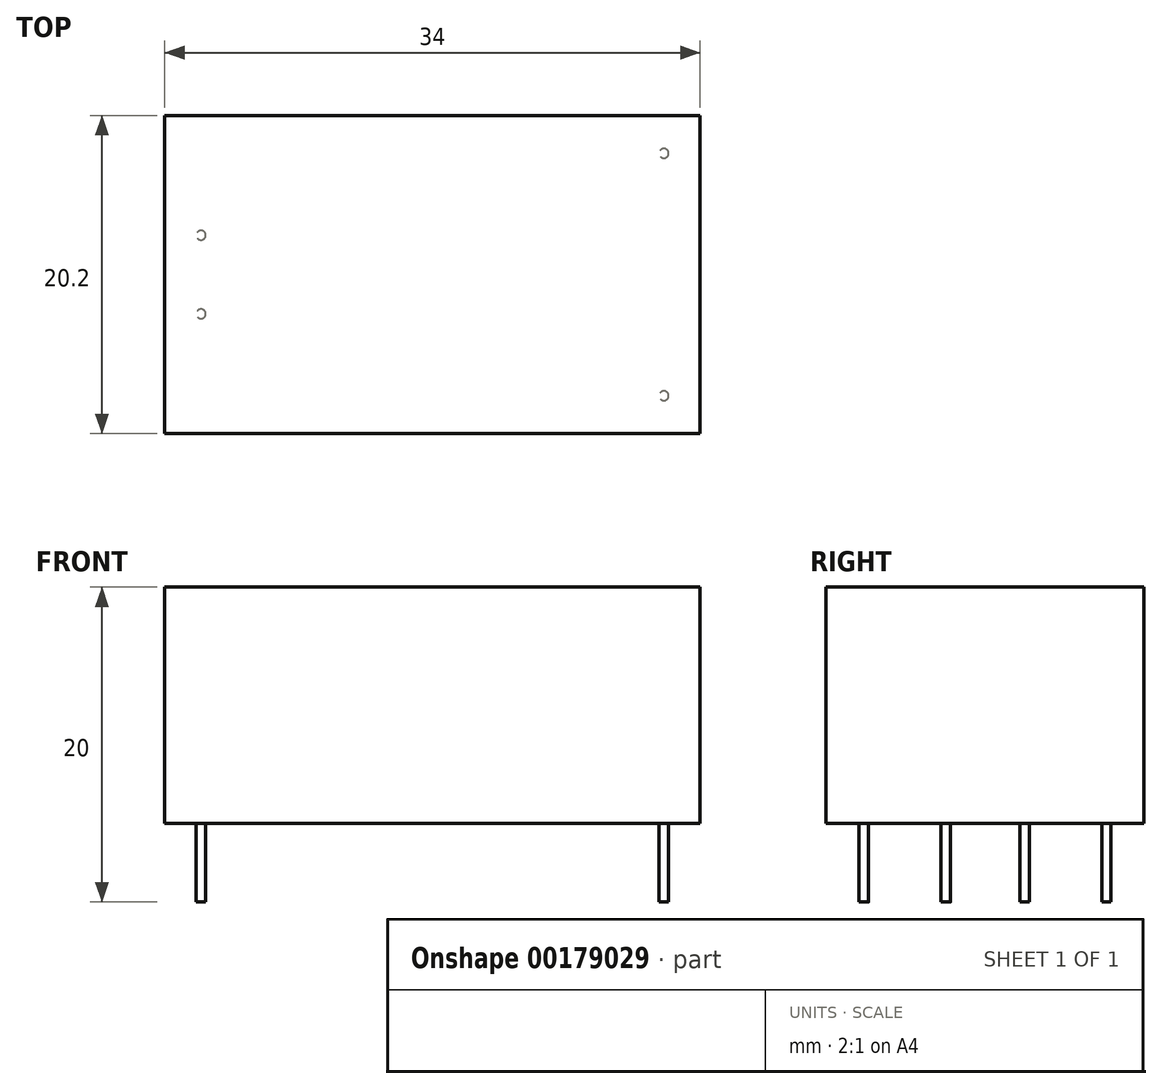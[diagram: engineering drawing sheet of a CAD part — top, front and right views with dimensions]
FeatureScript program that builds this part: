
annotation { "Feature Type Name" : "Feature", "Feature Type Description" : "" }
export const myFeature = defineFeature(function(context is Context, id is Id, definition is map)
    precondition{}
    {
        {
            var Q0;
            Q0=qCreatedBy(makeId("Top.planeOp"),FACE);
            var sketch = newSketch(context, id + "F0", { "sketchPlane" : qUnion([Q0])});
            skLineSegment(sketch, "E0.bottom", {"start": v(-17, 10.1) * mm, "end": v(17, 10.1) * mm});
            skLineSegment(sketch, "E0.top", {"start": v(-17, -10.1) * mm, "end": v(17, -10.1) * mm});
            skLineSegment(sketch, "E0.left", {"start": v(-17, 10.1) * mm, "end": v(-17, -10.1) * mm});
            skLineSegment(sketch, "E0.right", {"start": v(17, 10.1) * mm, "end": v(17, -10.1) * mm});
            skCircle(sketch, "E1", {"center": v(-14.7, 2.5) * mm, "radius": 0.3 * mm});
            skCircle(sketch, "E2", {"center": v(-14.7, -2.5) * mm, "radius": 0.3 * mm});
            skCircle(sketch, "E3", {"center": v(14.7, 7.7) * mm, "radius": 0.3 * mm});
            skCircle(sketch, "E4", {"center": v(14.7, -7.7) * mm, "radius": 0.3 * mm});
            skLineSegment(sketch, "E5", {"start": v(-14.7, 2.5) * mm, "end": v(-14.7, -2.5) * mm, "construction": true});
            skLineSegment(sketch, "E6", {"start": v(14.7, 7.7) * mm, "end": v(14.7, -7.7) * mm, "construction": true});
            skSolve(sketch);
        }
        {
            var Q0;
            Q0=makeQuery(id+"F0.imprint","IMPRINT",FACE,{"disambiguationData":[TD([[makeQuery(id+"F0.imprint","IMPRINT",EDGE,{"derivedFrom":sQuery(id+"F0.wireOp",EDGE,"E1")}),1.0]])]});
            var Q1;
            Q1=makeQuery(id+"F0.imprint","IMPRINT",FACE,{"disambiguationData":[TD([[makeQuery(id+"F0.imprint","IMPRINT",EDGE,{"derivedFrom":sQuery(id+"F0.wireOp",EDGE,"E0.bottom")}),-1.0]])]});
            var Q2;
            Q2=makeQuery(id+"F0.imprint","IMPRINT",FACE,{"disambiguationData":[TD([[makeQuery(id+"F0.imprint","IMPRINT",EDGE,{"derivedFrom":sQuery(id+"F0.wireOp",EDGE,"E3")}),1.0]])]});
            var Q3;
            Q3=makeQuery(id+"F0.imprint","IMPRINT",FACE,{"disambiguationData":[TD([[makeQuery(id+"F0.imprint","IMPRINT",EDGE,{"derivedFrom":sQuery(id+"F0.wireOp",EDGE,"E4")}),1.0]])]});
            var Q4;
            Q4=makeQuery(id+"F0.imprint","IMPRINT",FACE,{"disambiguationData":[TD([[makeQuery(id+"F0.imprint","IMPRINT",EDGE,{"derivedFrom":sQuery(id+"F0.wireOp",EDGE,"E2")}),1.0]])]});
            extrude(context, id + "F1", {"entities" : qUnion([Q0, Q1, Q2, Q3, Q4]), "depth" : 15 * mm});
        }
        {
            var Q0;
            Q0=makeQuery(id+"F0.imprint","IMPRINT",FACE,{"disambiguationData":[TD([[makeQuery(id+"F0.imprint","IMPRINT",EDGE,{"derivedFrom":sQuery(id+"F0.wireOp",EDGE,"E2")}),1.0]])]});
            var Q1;
            Q1=makeQuery(id+"F0.imprint","IMPRINT",FACE,{"disambiguationData":[TD([[makeQuery(id+"F0.imprint","IMPRINT",EDGE,{"derivedFrom":sQuery(id+"F0.wireOp",EDGE,"E1")}),1.0]])]});
            var Q2;
            Q2=makeQuery(id+"F0.imprint","IMPRINT",FACE,{"disambiguationData":[TD([[makeQuery(id+"F0.imprint","IMPRINT",EDGE,{"derivedFrom":sQuery(id+"F0.wireOp",EDGE,"E4")}),1.0]])]});
            var Q3;
            Q3=makeQuery(id+"F0.imprint","IMPRINT",FACE,{"disambiguationData":[TD([[makeQuery(id+"F0.imprint","IMPRINT",EDGE,{"derivedFrom":sQuery(id+"F0.wireOp",EDGE,"E3")}),1.0]])]});
            extrude(context, id + "F2", {"entities" : qUnion([Q0, Q1, Q2, Q3]), "oppositeDirection" : true, "depth" : 5 * mm});
        }
    });
